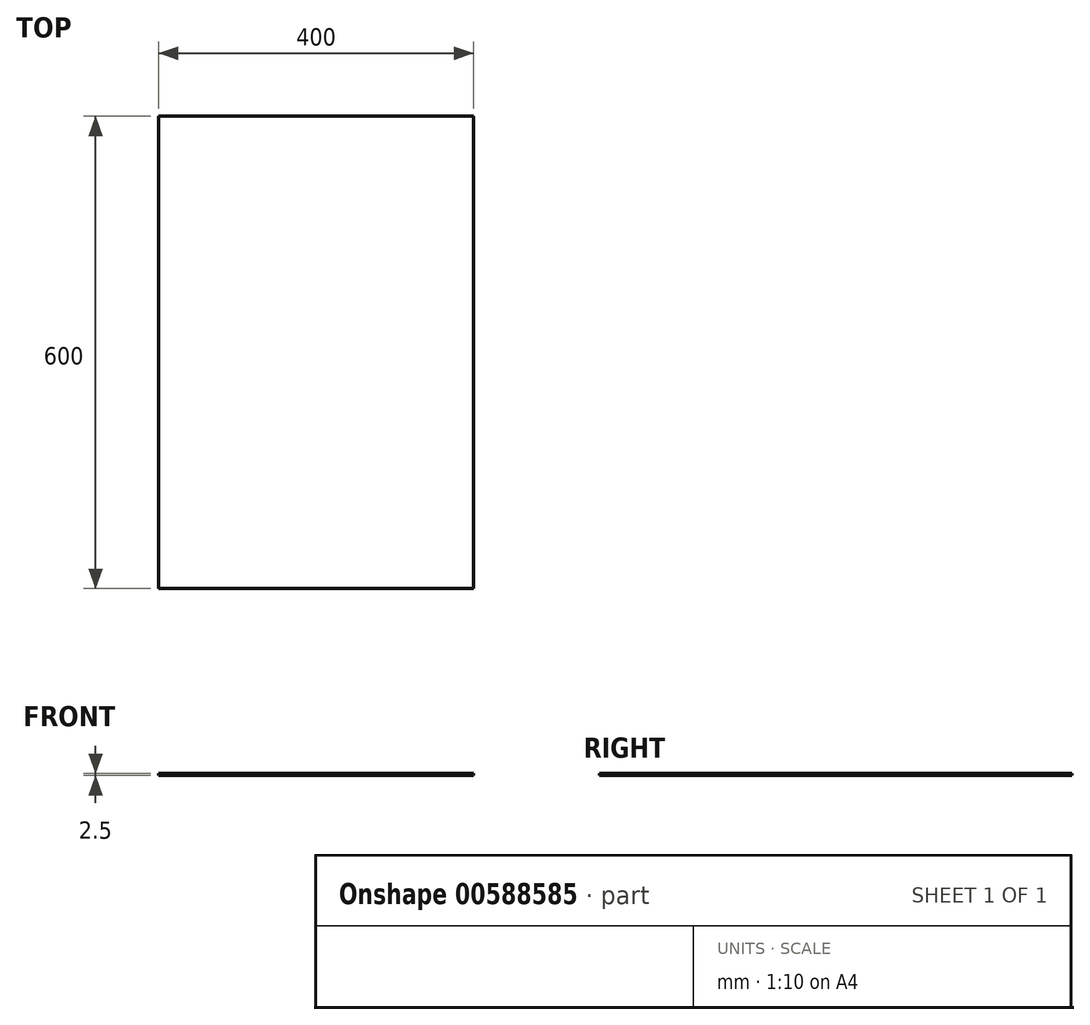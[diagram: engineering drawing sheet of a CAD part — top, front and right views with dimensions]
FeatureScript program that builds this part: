
annotation { "Feature Type Name" : "Feature", "Feature Type Description" : "" }
export const myFeature = defineFeature(function(context is Context, id is Id, definition is map)
    precondition{}
    {
        {
            var Q0;
            Q0=qCreatedBy(makeId("Top.planeOp"),FACE);
            var sketch = newSketch(context, id + "F0", { "sketchPlane" : qUnion([Q0])});
            skLineSegment(sketch, "E0.bottom", {"start": v(187.93, 300) * mm, "end": v(-212.07, 300) * mm});
            skLineSegment(sketch, "E0.top", {"start": v(187.93, -300) * mm, "end": v(-212.07, -300) * mm});
            skLineSegment(sketch, "E0.left", {"start": v(187.93, 300) * mm, "end": v(187.93, -300) * mm});
            skLineSegment(sketch, "E0.right", {"start": v(-212.07, 300) * mm, "end": v(-212.07, -300) * mm});
            skPoint(sketch, "E0.middle", {"position": v(-12.07, 0) * mm});
            skSolve(sketch);
        }
        {
            var Q0;
            Q0=makeQuery(id+"F0.imprint","IMPRINT",FACE,{"disambiguationData":[TD([[makeQuery(id+"F0.imprint","IMPRINT",EDGE,{"derivedFrom":sQuery(id+"F0.wireOp",EDGE,"E0.bottom")}),1.0]])]});
            extrude(context, id + "F1", {"entities" : qUnion([Q0]), "depth" : 2.5 * mm, "offsetDistance" : 25 * mm});
        }
    });
